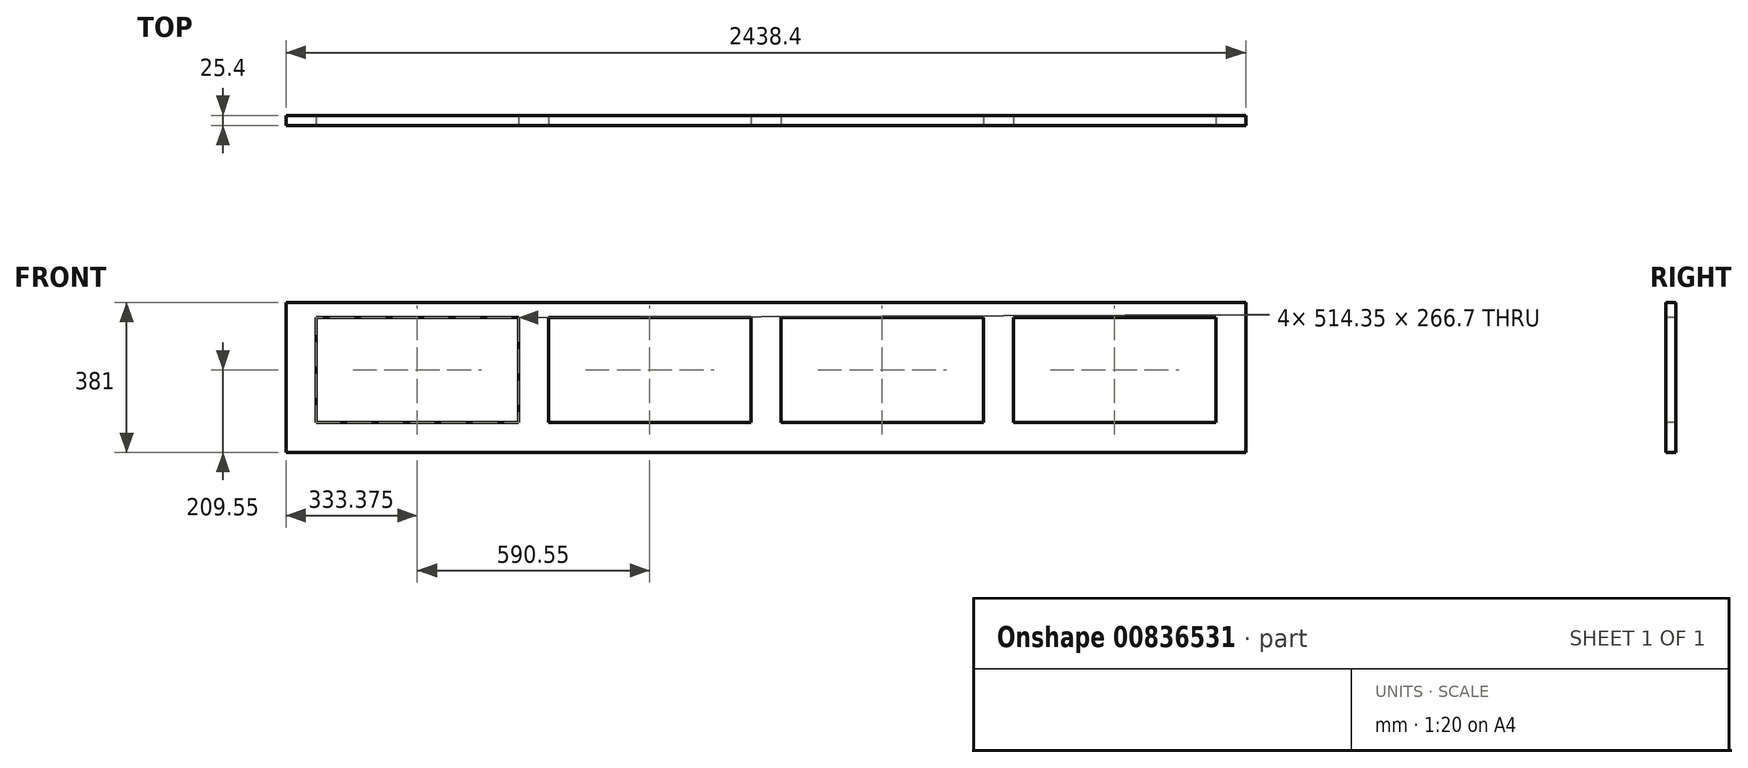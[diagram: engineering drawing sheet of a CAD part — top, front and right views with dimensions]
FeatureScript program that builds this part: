
annotation { "Feature Type Name" : "Feature", "Feature Type Description" : "" }
export const myFeature = defineFeature(function(context is Context, id is Id, definition is map)
    precondition{}
    {
        {
            var Q0;
            Q0=qCreatedBy(makeId("Front.planeOp"),FACE);
            var sketch = newSketch(context, id + "F0", { "sketchPlane" : qUnion([Q0])});
            skLineSegment(sketch, "E0.bottom", {"start": v(0, 0) * mm, "end": v(2438.4, 0) * mm});
            skLineSegment(sketch, "E0.top", {"start": v(0, 381) * mm, "end": v(2438.4, 381) * mm});
            skLineSegment(sketch, "E0.left", {"start": v(0, 0) * mm, "end": v(0, 381) * mm});
            skLineSegment(sketch, "E0.right", {"start": v(2438.4, 0) * mm, "end": v(2438.4, 381) * mm});
            skSolve(sketch);
        }
        {
            var Q0;
            Q0 = qSketchRegion(id + "F0", true);
            extrude(context, id + "F1", {"entities" : qUnion([Q0]), "depth" : 25.4 * mm, "offsetDistance" : 25.4 * mm});
        }
        {
            var Q0;
            Q0=makeQuery(id+"F1.opExtrude","CAP_FACE",FACE,{"disambiguationData":[OSD([sQuery(id+"F0.wireOp",EDGE,"E0.bottom"),sQuery(id+"F0.wireOp",EDGE,"E0.top"),sQuery(id+"F0.wireOp",EDGE,"E0.left"),sQuery(id+"F0.wireOp",EDGE,"E0.right")])],"isStart":false});
            var sketch = newSketch(context, id + "F2", { "sketchPlane" : qUnion([Q0])});
            skLineSegment(sketch, "E1.bottom", {"start": v(76.2, 342.9) * mm, "end": v(590.55, 342.9) * mm});
            skLineSegment(sketch, "E1.top", {"start": v(76.2, 76.2) * mm, "end": v(590.55, 76.2) * mm});
            skLineSegment(sketch, "E1.left", {"start": v(76.2, 342.9) * mm, "end": v(76.2, 76.2) * mm});
            skLineSegment(sketch, "E1.right", {"start": v(590.55, 342.9) * mm, "end": v(590.55, 76.2) * mm});
            skLineSegment(sketch, "E2.bottom", {"start": v(666.75, 342.9) * mm, "end": v(1181.1, 342.9) * mm});
            skLineSegment(sketch, "E2.top", {"start": v(666.75, 76.2) * mm, "end": v(1181.1, 76.2) * mm});
            skLineSegment(sketch, "E2.left", {"start": v(666.75, 342.9) * mm, "end": v(666.75, 76.2) * mm});
            skLineSegment(sketch, "E2.right", {"start": v(1181.1, 342.9) * mm, "end": v(1181.1, 76.2) * mm});
            skLineSegment(sketch, "E3.bottom", {"start": v(1257.3, 342.9) * mm, "end": v(1771.65, 342.9) * mm});
            skLineSegment(sketch, "E3.top", {"start": v(1257.3, 76.2) * mm, "end": v(1771.65, 76.2) * mm});
            skLineSegment(sketch, "E3.left", {"start": v(1257.3, 342.9) * mm, "end": v(1257.3, 76.2) * mm});
            skLineSegment(sketch, "E3.right", {"start": v(1771.65, 342.9) * mm, "end": v(1771.65, 76.2) * mm});
            skLineSegment(sketch, "E4.bottom", {"start": v(1847.85, 342.9) * mm, "end": v(2362.2, 342.9) * mm});
            skLineSegment(sketch, "E4.top", {"start": v(1847.85, 76.2) * mm, "end": v(2362.2, 76.2) * mm});
            skLineSegment(sketch, "E4.left", {"start": v(1847.85, 342.9) * mm, "end": v(1847.85, 76.2) * mm});
            skLineSegment(sketch, "E4.right", {"start": v(2362.2, 342.9) * mm, "end": v(2362.2, 76.2) * mm});
            skLineSegment(sketch, "E5", {"start": v(590.55, 209.55) * mm, "end": v(666.75, 209.55) * mm, "construction": true});
            skLineSegment(sketch, "E6", {"start": v(1181.1, 209.55) * mm, "end": v(1257.3, 209.55) * mm, "construction": true});
            skLineSegment(sketch, "E7", {"start": v(1771.65, 209.55) * mm, "end": v(1847.85, 209.55) * mm, "construction": true});
            skSolve(sketch);
        }
        {
            var Q0;
            Q0 = qSketchRegion(id + "F2", true);
            extrude(context, id + "F3", {"entities" : qUnion([Q0]), "operationType" : NewBodyOperationType.REMOVE, "oppositeDirection" : true, "depth" : 25.4 * mm, "offsetDistance" : 25.4 * mm});
        }
    });
